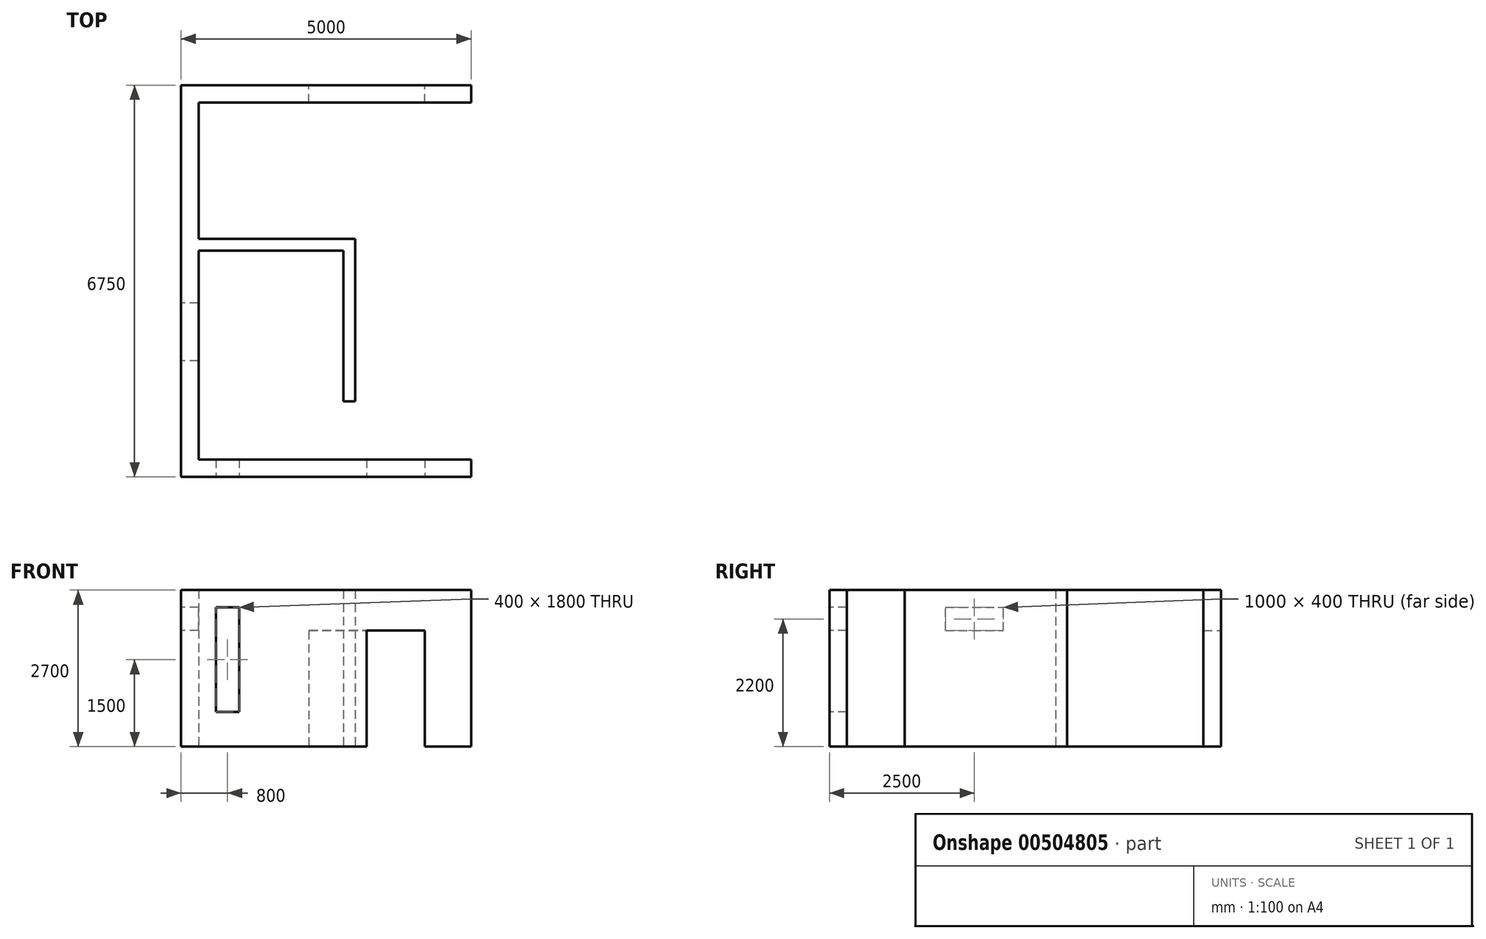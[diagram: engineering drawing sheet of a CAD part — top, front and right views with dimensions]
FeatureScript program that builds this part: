
annotation { "Feature Type Name" : "Feature", "Feature Type Description" : "" }
export const myFeature = defineFeature(function(context is Context, id is Id, definition is map)
    precondition{}
    {
        {
            var Q0;
            Q0=qCreatedBy(makeId("Top.planeOp"),FACE);
            var sketch = newSketch(context, id + "F0", { "sketchPlane" : qUnion([Q0])});
            skLineSegment(sketch, "E0.bottom", {"start": v(0, 0) * mm, "end": v(-5000, 0) * mm});
            skLineSegment(sketch, "E0.top", {"start": v(0, 6750) * mm, "end": v(-5000, 6750) * mm});
            skLineSegment(sketch, "E0.left", {"start": v(0, 0) * mm, "end": v(0, 6750) * mm});
            skLineSegment(sketch, "E0.right", {"start": v(-5000, 0) * mm, "end": v(-5000, 6750) * mm});
            skLineSegment(sketch, "E1.0", {"start": v(0, 6450) * mm, "end": v(-4700, 6450) * mm});
            skLineSegment(sketch, "E1.1", {"start": v(-4700, 300) * mm, "end": v(-4700, 6450) * mm});
            skLineSegment(sketch, "E1.2", {"start": v(0, 300) * mm, "end": v(-4700, 300) * mm});
            skPoint(sketch, "E2", {"position": v(-800, 0) * mm});
            skLineSegment(sketch, "E3", {"start": v(-4700, 300) * mm, "end": v(-4700, 1300) * mm});
            skLineSegment(sketch, "E4.bottom", {"start": v(-4700, 1300) * mm, "end": v(-2200, 1300) * mm});
            skLineSegment(sketch, "E4.top", {"start": v(-4700, 3900) * mm, "end": v(-2200, 3900) * mm});
            skLineSegment(sketch, "E4.left", {"start": v(-4700, 1300) * mm, "end": v(-4700, 3900) * mm});
            skLineSegment(sketch, "E4.right", {"start": v(-2200, 1300) * mm, "end": v(-2200, 3900) * mm});
            skLineSegment(sketch, "E5.0", {"start": v(-4700, 4100) * mm, "end": v(-2000, 4100) * mm});
            skLineSegment(sketch, "E5.1", {"start": v(-2000, 1300) * mm, "end": v(-2000, 4100) * mm});
            skLineSegment(sketch, "E6", {"start": v(-2200, 1300) * mm, "end": v(-2000, 1300) * mm});
            skSolve(sketch);
        }
        {
            var Q0;
            {var subQ3=sQuery(id+"F0.wireOp",EDGE,"E0.bottom");Q0=makeQuery(id+"F0.imprint","IMPRINT",FACE,{"disambiguationData":[TD([[makeQuery(id+"F0.imprint","IMPRINT",EDGE,{"derivedFrom":subQ3}),-1.0]])]});}
            extrude(context, id + "F1", {"entities" : qUnion([Q0]), "depth" : 2700 * mm, "offsetDistance" : 25 * mm});
        }
        {
            var Q0;
            Q0=makeQuery(id+"F1.opExtrude","SWEPT_FACE",FACE,{"disambiguationData":[OSD([sQuery(id+"F0.wireOp",EDGE,"E0.bottom")])]});
            var sketch = newSketch(context, id + "F2", { "sketchPlane" : qUnion([Q0])});
            skLineSegment(sketch, "E7", {"start": v(0, 0) * mm, "end": v(-800, 0) * mm});
            skLineSegment(sketch, "E8.bottom", {"start": v(-800, 0) * mm, "end": v(-1800, 0) * mm});
            skLineSegment(sketch, "E8.top", {"start": v(-800, 2000) * mm, "end": v(-1800, 2000) * mm});
            skLineSegment(sketch, "E8.left", {"start": v(-800, 0) * mm, "end": v(-800, 2000) * mm});
            skLineSegment(sketch, "E8.right", {"start": v(-1800, 0) * mm, "end": v(-1800, 2000) * mm});
            skLineSegment(sketch, "E9", {"start": v(-5000, 0) * mm, "end": v(-4400, 0) * mm});
            skLineSegment(sketch, "E10", {"start": v(-4400, 0) * mm, "end": v(-4400, 600) * mm});
            skLineSegment(sketch, "E11.bottom", {"start": v(-4400, 600) * mm, "end": v(-4000, 600) * mm});
            skLineSegment(sketch, "E11.top", {"start": v(-4400, 2400) * mm, "end": v(-4000, 2400) * mm});
            skLineSegment(sketch, "E11.left", {"start": v(-4400, 600) * mm, "end": v(-4400, 2400) * mm});
            skLineSegment(sketch, "E11.right", {"start": v(-4000, 600) * mm, "end": v(-4000, 2400) * mm});
            skSolve(sketch);
        }
        {
            var Q0;
            Q0=makeQuery(id+"F2.imprint","IMPRINT",FACE,{"disambiguationData":[TD([[makeQuery(id+"F2.imprint","IMPRINT",EDGE,{"derivedFrom":sQuery(id+"F2.wireOp",EDGE,"E8.bottom")}),-1.0]])]});
            extrude(context, id + "F3", {"entities" : qUnion([Q0]), "operationType" : NewBodyOperationType.REMOVE, "oppositeDirection" : true, "depth" : 400 * mm});
        }
        {
            var Q0;
            Q0=makeQuery(id+"F2.imprint","IMPRINT",FACE,{"disambiguationData":[TD([[makeQuery(id+"F2.imprint","IMPRINT",EDGE,{"derivedFrom":sQuery(id+"F2.wireOp",EDGE,"E11.bottom")}),1.0]])]});
            extrude(context, id + "F4", {"entities" : qUnion([Q0]), "operationType" : NewBodyOperationType.REMOVE, "oppositeDirection" : true, "depth" : 400 * mm});
        }
        {
            var Q0;
            Q0=makeQuery(id+"F1.opExtrude","SWEPT_FACE",FACE,{"disambiguationData":[OSD([sQuery(id+"F0.wireOp",EDGE,"E0.top")])]});
            var sketch = newSketch(context, id + "F5", { "sketchPlane" : qUnion([Q0])});
            skLineSegment(sketch, "E12", {"start": v(0, 0) * mm, "end": v(800, 0) * mm});
            skLineSegment(sketch, "E13.bottom", {"start": v(800, 0) * mm, "end": v(2800, 0) * mm});
            skLineSegment(sketch, "E13.top", {"start": v(800, 2000) * mm, "end": v(2800, 2000) * mm});
            skLineSegment(sketch, "E13.left", {"start": v(800, 0) * mm, "end": v(800, 2000) * mm});
            skLineSegment(sketch, "E13.right", {"start": v(2800, 0) * mm, "end": v(2800, 2000) * mm});
            skSolve(sketch);
        }
        {
            var Q0;
            Q0=makeQuery(id+"F5.imprint","IMPRINT",FACE,{"disambiguationData":[TD([[makeQuery(id+"F5.imprint","IMPRINT",EDGE,{"derivedFrom":sQuery(id+"F5.wireOp",EDGE,"E13.bottom")}),1.0]])]});
            extrude(context, id + "F6", {"entities" : qUnion([Q0]), "operationType" : NewBodyOperationType.REMOVE, "oppositeDirection" : true, "depth" : 400 * mm, "offsetDistance" : 25 * mm});
        }
        {
            var Q0;
            {var subQ1=sQuery(id+"F0.wireOp",EDGE,"E4.top");Q0=makeQuery(id+"F0.imprint","IMPRINT",FACE,{"disambiguationData":[TD([[makeQuery(id+"F0.imprint","IMPRINT",EDGE,{"derivedFrom":subQ1}),1.0]])]});}
            extrude(context, id + "F7", {"entities" : qUnion([Q0]), "operationType" : NewBodyOperationType.ADD, "depth" : 2700 * mm});
        }
        {
            var Q0;
            Q0=makeQuery(id+"F1.opExtrude","SWEPT_FACE",FACE,{"disambiguationData":[OSD([sQuery(id+"F0.wireOp",EDGE,"E0.right")])]});
            var sketch = newSketch(context, id + "F8", { "sketchPlane" : qUnion([Q0])});
            skLineSegment(sketch, "E14", {"start": v(0, 0) * mm, "end": v(-2000, 0) * mm});
            skLineSegment(sketch, "E15", {"start": v(-2000, 0) * mm, "end": v(-2000, 2000) * mm});
            skLineSegment(sketch, "E16.bottom", {"start": v(-2000, 2000) * mm, "end": v(-3000, 2000) * mm});
            skLineSegment(sketch, "E16.top", {"start": v(-2000, 2400) * mm, "end": v(-3000, 2400) * mm});
            skLineSegment(sketch, "E16.left", {"start": v(-2000, 2000) * mm, "end": v(-2000, 2400) * mm});
            skLineSegment(sketch, "E16.right", {"start": v(-3000, 2000) * mm, "end": v(-3000, 2400) * mm});
            skSolve(sketch);
        }
        {
            var Q0;
            Q0=makeQuery(id+"F8.imprint","IMPRINT",FACE,{"disambiguationData":[TD([[makeQuery(id+"F8.imprint","IMPRINT",EDGE,{"derivedFrom":sQuery(id+"F8.wireOp",EDGE,"E16.bottom")}),-1.0]])]});
            extrude(context, id + "F9", {"entities" : qUnion([Q0]), "operationType" : NewBodyOperationType.REMOVE, "oppositeDirection" : true, "depth" : 400 * mm});
        }
    });
